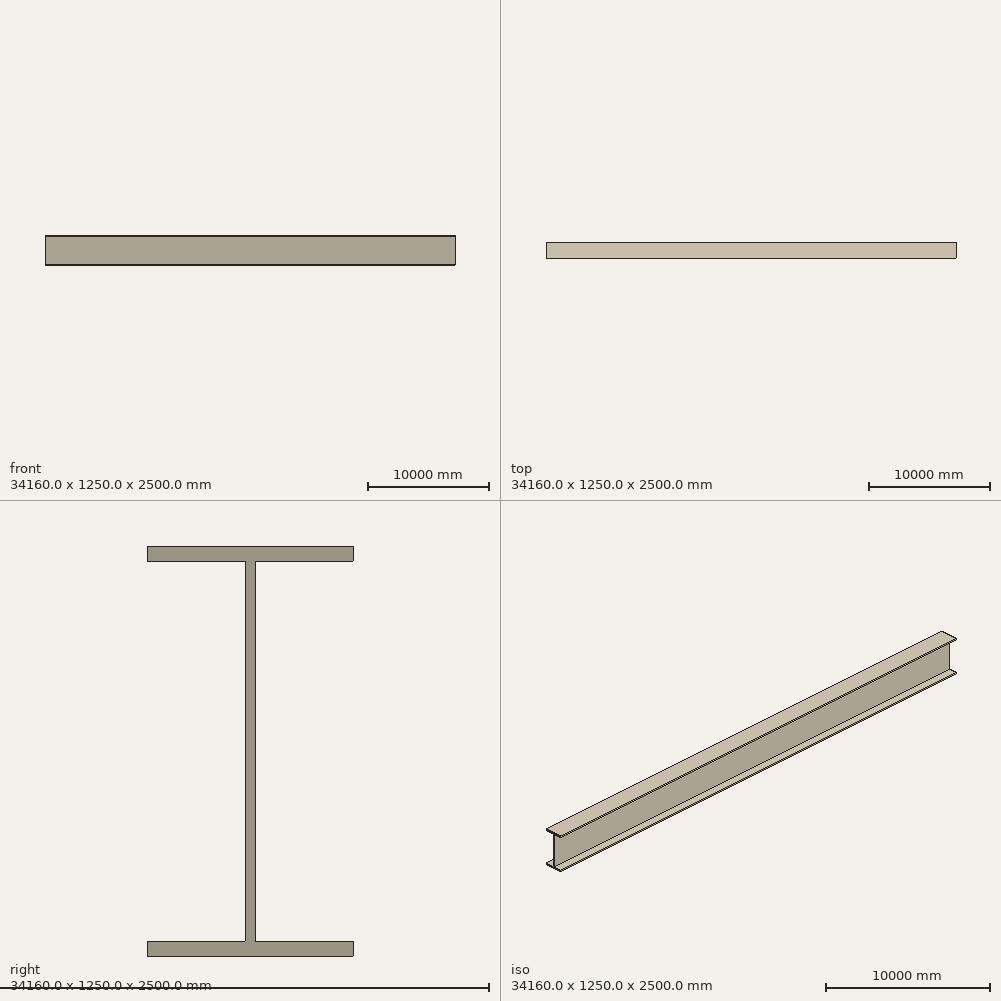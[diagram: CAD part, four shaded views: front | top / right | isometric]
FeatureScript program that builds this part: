
annotation { "Feature Type Name" : "Feature", "Feature Type Description" : "" }
export const myFeature = defineFeature(function(context is Context, id is Id, definition is map)
    precondition{}
    {
        {
            var Q0;
            Q0=qCreatedBy(makeId("Right.planeOp"),FACE);
            var sketch = newSketch(context, id + "F0", { "sketchPlane" : qUnion([Q0])});
            skLineSegment(sketch, "E0", {"start": v(0, 0) * mm, "end": v(0, 2500) * mm});
            skLineSegment(sketch, "E1", {"start": v(0, 2500) * mm, "end": v(-625, 2500) * mm});
            skLineSegment(sketch, "E2", {"start": v(-625, 2500) * mm, "end": v(-625, 2410) * mm});
            skLineSegment(sketch, "E3", {"start": v(-625, 2410) * mm, "end": v(-30, 2410) * mm});
            skLineSegment(sketch, "E4", {"start": v(-30, 2410) * mm, "end": v(-30, 90) * mm});
            skLineSegment(sketch, "E5", {"start": v(-30, 90) * mm, "end": v(-625, 90) * mm});
            skLineSegment(sketch, "E6", {"start": v(-625, 90) * mm, "end": v(-625, 0) * mm});
            skLineSegment(sketch, "E7", {"start": v(-625, 0) * mm, "end": v(0, 0) * mm});
            skLineSegment(sketch, "E8.MirrorCS", {"start": v(625, 2500) * mm, "end": v(625, 2410) * mm});
            skLineSegment(sketch, "E9.MirrorCS", {"start": v(625, 90) * mm, "end": v(625, 0) * mm});
            skLineSegment(sketch, "E10.MirrorCS", {"start": v(0, 2500) * mm, "end": v(625, 2500) * mm});
            skLineSegment(sketch, "E11.MirrorCS", {"start": v(625, 2410) * mm, "end": v(30, 2410) * mm});
            skLineSegment(sketch, "E12.MirrorCS", {"start": v(625, 0) * mm, "end": v(0, 0) * mm});
            skLineSegment(sketch, "E13.MirrorCS", {"start": v(30, 90) * mm, "end": v(625, 90) * mm});
            skLineSegment(sketch, "E14.MirrorCS", {"start": v(30, 2410) * mm, "end": v(30, 90) * mm});
            skSolve(sketch);
        }
        {
            var Q0;
            Q0=makeQuery(id+"F0.imprint","IMPRINT",FACE,{"disambiguationData":[TD([[makeQuery(id+"F0.imprint","IMPRINT",EDGE,{"derivedFrom":sQuery(id+"F0.wireOp",EDGE,"E0")}),1.0]])]});
            var Q1;
            Q1=makeQuery(id+"F0.imprint","IMPRINT",FACE,{"disambiguationData":[TD([[makeQuery(id+"F0.imprint","IMPRINT",EDGE,{"derivedFrom":sQuery(id+"F0.wireOp",EDGE,"E0")}),-1.0]])]});
            extrude(context, id + "F1", {"entities" : qUnion([Q0, Q1]), "oppositeDirection" : true, "depth" : 34160 * mm, "offsetDistance" : 25 * mm});
        }
    });
